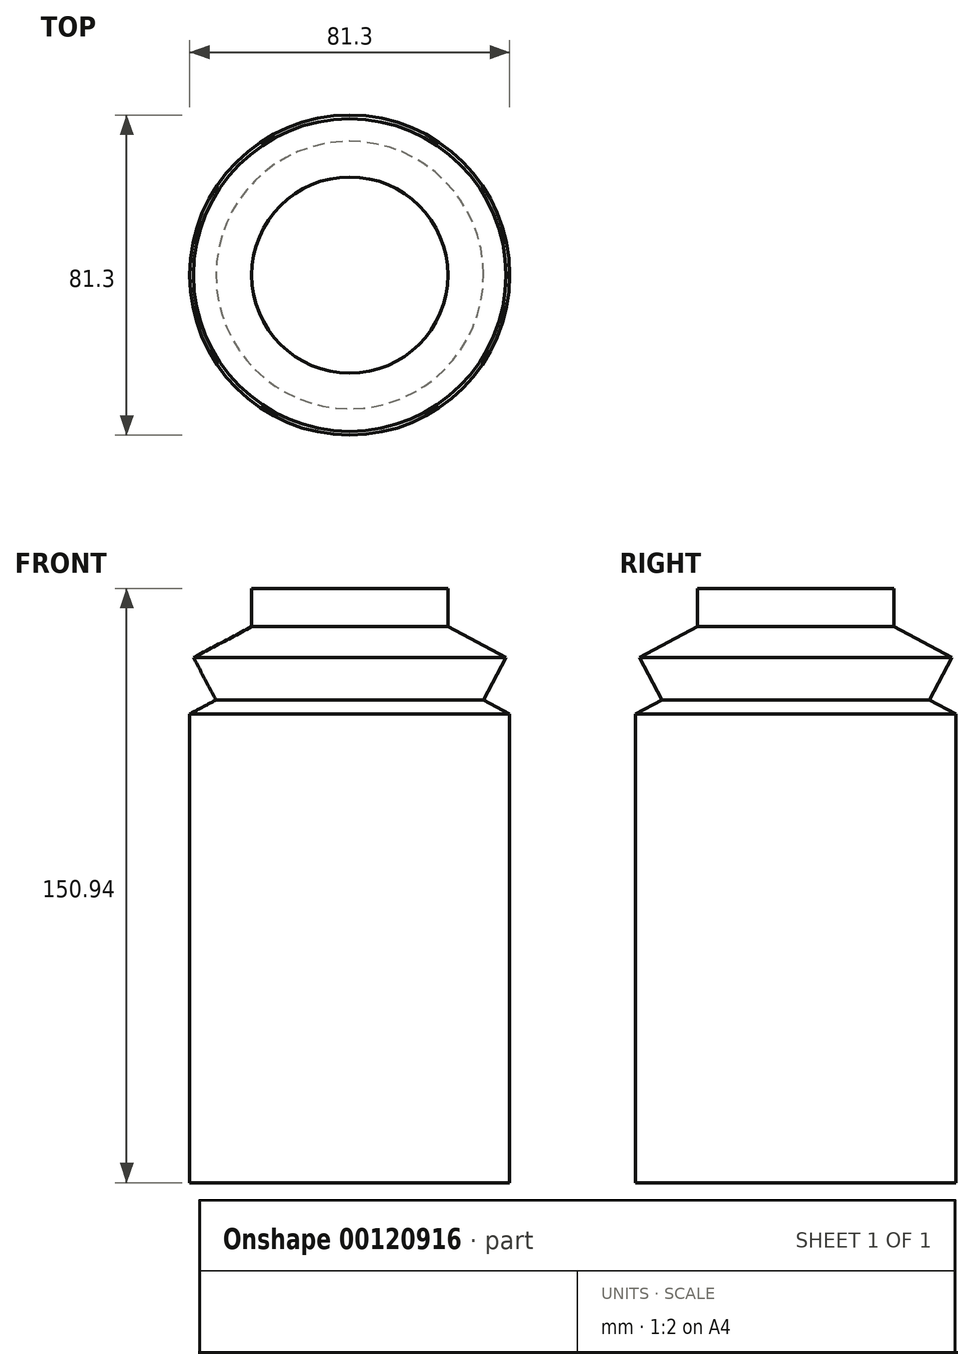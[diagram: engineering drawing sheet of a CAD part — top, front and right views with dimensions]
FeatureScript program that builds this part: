
annotation { "Feature Type Name" : "Feature", "Feature Type Description" : "" }
export const myFeature = defineFeature(function(context is Context, id is Id, definition is map)
    precondition{}
    {
        {
            var Q0;
            Q0=qCreatedBy(makeId("Front.planeOp"),FACE);
            var sketch = newSketch(context, id + "F0", { "sketchPlane" : qUnion([Q0])});
            skLineSegment(sketch, "E0", {"start": v(0, 75.47) * mm, "end": v(24.93, 75.47) * mm});
            skLineSegment(sketch, "E1", {"start": v(24.93, 75.47) * mm, "end": v(24.93, 65.78) * mm});
            skLineSegment(sketch, "E2", {"start": v(24.93, 65.78) * mm, "end": v(39.7, 57.93) * mm});
            skLineSegment(sketch, "E3", {"start": v(39.7, 57.93) * mm, "end": v(33.98, 47.16) * mm});
            skLineSegment(sketch, "E4", {"start": v(33.98, 47.16) * mm, "end": v(40.65, 43.62) * mm});
            skLineSegment(sketch, "E5", {"start": v(40.65, 43.62) * mm, "end": v(40.65, -75.47) * mm});
            skLineSegment(sketch, "E6", {"start": v(40.65, -75.47) * mm, "end": v(0, -75.47) * mm});
            skLineSegment(sketch, "E7", {"start": v(0, -75.47) * mm, "end": v(0, 75.47) * mm});
            skSolve(sketch);
        }
        {
            var Q0;
            Q0=makeQuery(id+"F0.imprint","IMPRINT",FACE,{"disambiguationData":[TD([[makeQuery(id+"F0.imprint","IMPRINT",EDGE,{"derivedFrom":sQuery(id+"F0.wireOp",EDGE,"E0")}),-1.0]])]});
            var Q1;
            Q1=sQuery(id+"F0.wireOp",EDGE,"E7");
            revolve(context, id + "F1", {"entities" : qUnion([Q0]), "axis" : qUnion([Q1]), "revolveType" : RevolveType.FULL});
        }
    });
